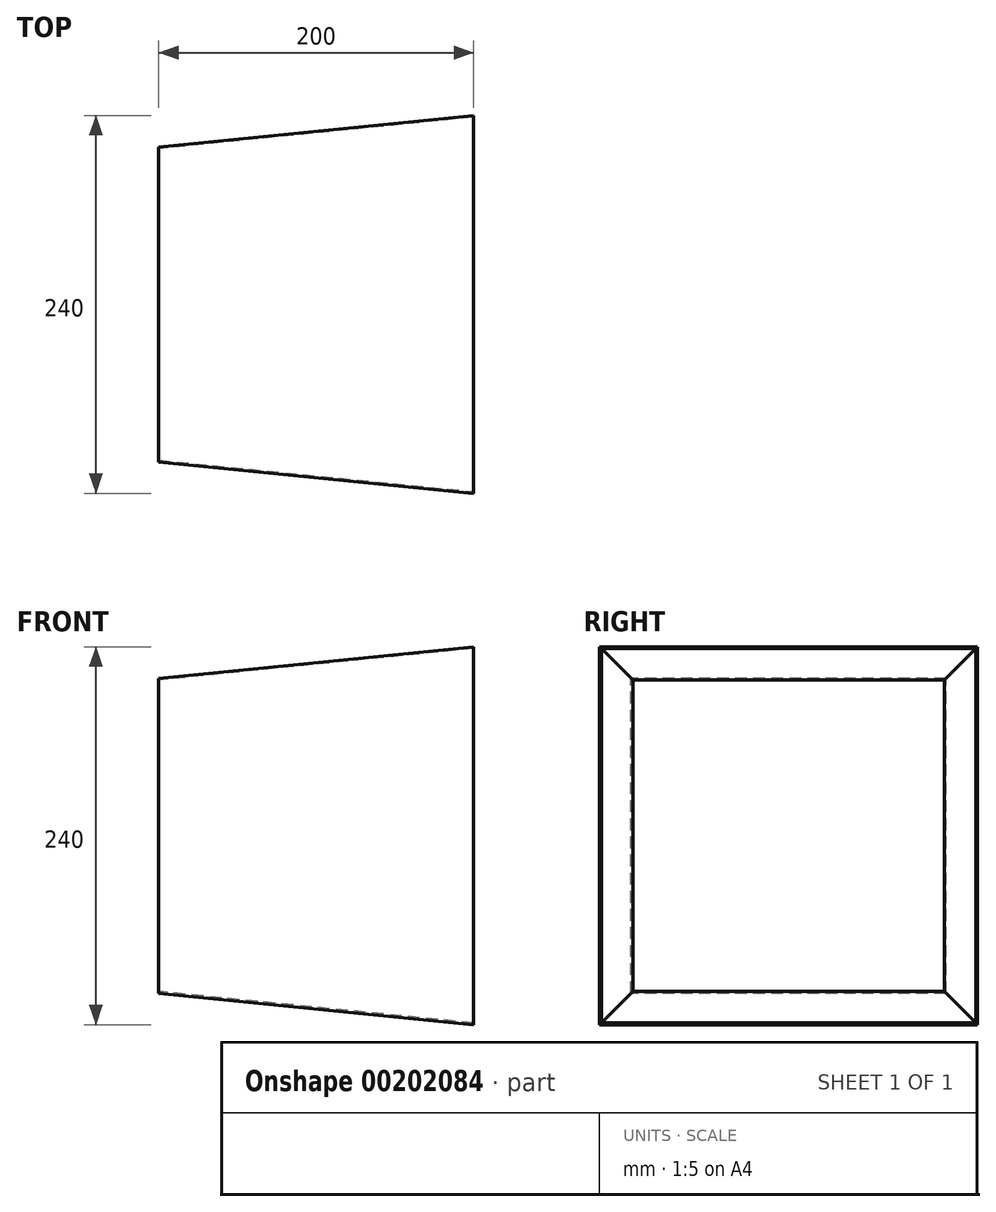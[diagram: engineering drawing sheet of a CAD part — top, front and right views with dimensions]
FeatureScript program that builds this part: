
annotation { "Feature Type Name" : "Feature", "Feature Type Description" : "" }
export const myFeature = defineFeature(function(context is Context, id is Id, definition is map)
    precondition{}
    {
        {
            var Q0;
            Q0=qCreatedBy(makeId("Right.planeOp"),FACE);
            var sketch = newSketch(context, id + "F0", { "sketchPlane" : qUnion([Q0])});
            skLineSegment(sketch, "E0.bottom", {"start": v(100, -100) * mm, "end": v(-100, -100) * mm});
            skLineSegment(sketch, "E0.top", {"start": v(100, 100) * mm, "end": v(-100, 100) * mm});
            skLineSegment(sketch, "E0.left", {"start": v(100, -100) * mm, "end": v(100, 100) * mm});
            skLineSegment(sketch, "E0.right", {"start": v(-100, -100) * mm, "end": v(-100, 100) * mm});
            skPoint(sketch, "E0.middle", {"position": v(0, 0) * mm});
            skSolve(sketch);
        }
        {
            var Q0;
            Q0=makeQuery(id+"F0.imprint","IMPRINT",FACE,{"disambiguationData":[TD([[makeQuery(id+"F0.imprint","IMPRINT",EDGE,{"derivedFrom":sQuery(id+"F0.wireOp",EDGE,"E0.bottom")}),-1.0]])]});
            cPlane(context, id + "F1", {"entities" : qUnion([Q0]), "cplaneType" : CPlaneType.OFFSET, "offset" : 200 * mm, "width" : 150 * mm, "height" : 150 * mm});
        }
        {
            var Q0;
            Q0=qCreatedBy(id+"F1.planeOp",FACE);
            var sketch = newSketch(context, id + "F2", { "sketchPlane" : qUnion([Q0])});
            skLineSegment(sketch, "E1.bottom", {"start": v(120, -120) * mm, "end": v(-120, -120) * mm});
            skLineSegment(sketch, "E1.top", {"start": v(120, 120) * mm, "end": v(-120, 120) * mm});
            skLineSegment(sketch, "E1.left", {"start": v(120, -120) * mm, "end": v(120, 120) * mm});
            skLineSegment(sketch, "E1.right", {"start": v(-120, -120) * mm, "end": v(-120, 120) * mm});
            skPoint(sketch, "E1.middle", {"position": v(0, 0) * mm});
            skSolve(sketch);
        }
        {
            var Q0;
            Q0=makeQuery(id+"F0.imprint","IMPRINT",FACE,{"disambiguationData":[TD([[makeQuery(id+"F0.imprint","IMPRINT",EDGE,{"derivedFrom":sQuery(id+"F0.wireOp",EDGE,"E0.bottom")}),-1.0]])]});
            var Q1;
            Q1=makeQuery(id+"F2.imprint","IMPRINT",FACE,{"disambiguationData":[TD([[makeQuery(id+"F2.imprint","IMPRINT",EDGE,{"derivedFrom":sQuery(id+"F2.wireOp",EDGE,"E1.bottom")}),-1.0]])]});
            loft(context, id + "F3", {"sheetProfilesArray" : [{ "sheetProfileEntities" : qUnion([Q0]) }, { "sheetProfileEntities" : qUnion([Q1]) }]});
        }
        {
            var Q0;
            Q0=makeQuery(id+"F3.opLoft","CAP_FACE",FACE,{"disambiguationData":[OSD([makeQuery(id+"F2.imprint","IMPRINT",FACE,{"disambiguationData":[TD([[makeQuery(id+"F2.imprint","IMPRINT",EDGE,{"derivedFrom":sQuery(id+"F2.wireOp",EDGE,"E1.bottom")}),-1.0]])]})])],"isStart":true});
            var Q1;
            Q1=makeQuery(id+"F3.opLoft","CAP_FACE",FACE,{"disambiguationData":[OSD([makeQuery(id+"F0.imprint","IMPRINT",FACE,{"disambiguationData":[TD([[makeQuery(id+"F0.imprint","IMPRINT",EDGE,{"derivedFrom":sQuery(id+"F0.wireOp",EDGE,"E0.bottom")}),-1.0]])]})])],"isStart":true});
            shell(context, id + "F4", {"entities" : qUnion([Q0, Q1]), "thickness" : 1 * mm});
        }
    });
